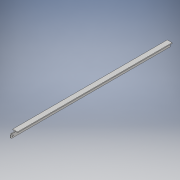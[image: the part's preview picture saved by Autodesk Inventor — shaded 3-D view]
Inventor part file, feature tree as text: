
AUTODESK INVENTOR PART (.ipt)
format: ipt  version: 2019 (Build 230136000, 136)  size: 166,912 bytes
history: native  units: mm
features: extrude x3, sketch x3, projected_geometry x2, fillet x1, chamfer x1
ambient origin geometry x8: Origin, YZ Plane, XZ Plane, XY Plane, X Axis, Y Axis, Z Axis, Center Point
bodies: Solide1 (feature_tree)
feature tree (10):
  extrude  "Extrusion1"  Depth=30.0mm
  extrude  "Extrusion9"  Depth=5.0mm
  fillet  "Congé2"  Radius=5.0mm
  extrude  "Extrusion10"  Depth=30.0mm
  chamfer  "Chanfrein1"  Distance=1000.0mm
  sketch  "Esquisse1"
  sketch  "Esquisse10"
  projected_geometry  "Boucle projetée9"
  sketch  "Esquisse11"
  projected_geometry  "Boucle projetée10"
